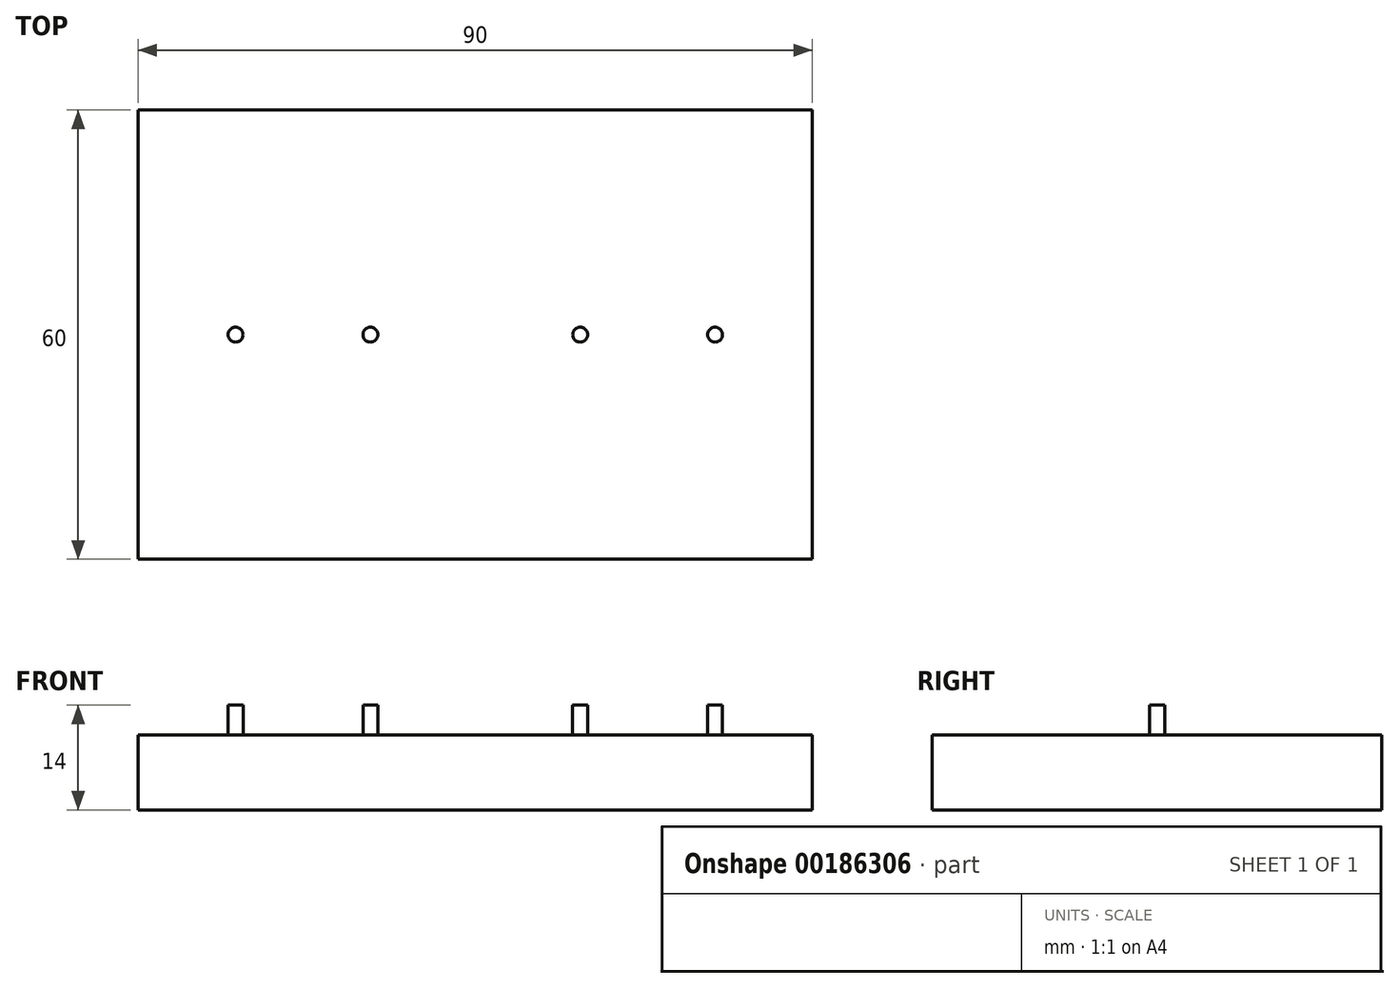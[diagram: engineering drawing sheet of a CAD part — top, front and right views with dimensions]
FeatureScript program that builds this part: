
annotation { "Feature Type Name" : "Feature", "Feature Type Description" : "" }
export const myFeature = defineFeature(function(context is Context, id is Id, definition is map)
    precondition{}
    {
        {
            var Q0;
            Q0=qCreatedBy(makeId("Top.planeOp"),FACE);
            var sketch = newSketch(context, id + "F0", { "sketchPlane" : qUnion([Q0])});
            skLineSegment(sketch, "E0.bottom", {"start": v(45, -30) * mm, "end": v(-45, -30) * mm});
            skLineSegment(sketch, "E0.top", {"start": v(45, 30) * mm, "end": v(-45, 30) * mm});
            skLineSegment(sketch, "E0.left", {"start": v(45, -30) * mm, "end": v(45, 30) * mm});
            skLineSegment(sketch, "E0.right", {"start": v(-45, -30) * mm, "end": v(-45, 30) * mm});
            skPoint(sketch, "E0.middle", {"position": v(0, 0) * mm});
            skSolve(sketch);
        }
        {
            var Q0;
            Q0 = qSketchRegion(id + "F0", true);
            extrude(context, id + "F1", {"entities" : qUnion([Q0]), "depth" : 10 * mm});
        }
        {
            var Q0;
            Q0=makeQuery(id+"F1.opExtrude","CAP_FACE",FACE,{"disambiguationData":[OSD([sQuery(id+"F0.wireOp",EDGE,"E0.bottom"),sQuery(id+"F0.wireOp",EDGE,"E0.top"),sQuery(id+"F0.wireOp",EDGE,"E0.left"),sQuery(id+"F0.wireOp",EDGE,"E0.right")])],"isStart":false});
            var sketch = newSketch(context, id + "F2", { "sketchPlane" : qUnion([Q0])});
            skCircle(sketch, "E1", {"center": v(-14, 0) * mm, "radius": 1 * mm});
            skCircle(sketch, "E2", {"center": v(14, 0) * mm, "radius": 1 * mm});
            skCircle(sketch, "E3", {"center": v(-32, 0) * mm, "radius": 1 * mm});
            skCircle(sketch, "E4", {"center": v(32, 0) * mm, "radius": 1 * mm});
            skSolve(sketch);
        }
        {
            var Q0;
            Q0 = qSketchRegion(id + "F2", true);
            extrude(context, id + "F3", {"entities" : qUnion([Q0]), "operationType" : NewBodyOperationType.ADD, "depth" : 4 * mm});
        }
    });
